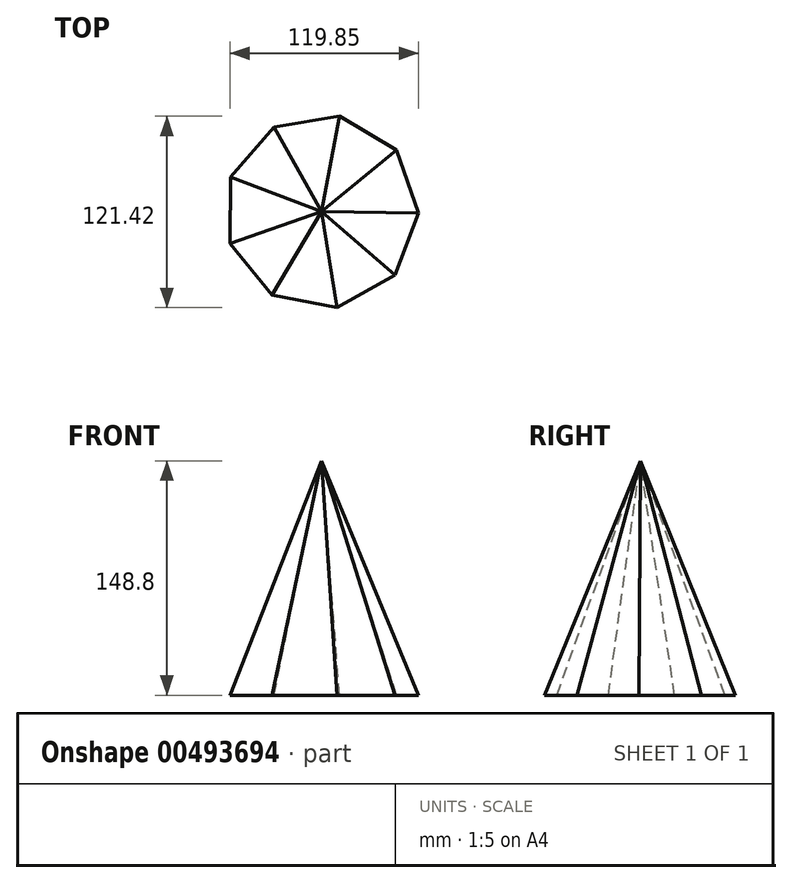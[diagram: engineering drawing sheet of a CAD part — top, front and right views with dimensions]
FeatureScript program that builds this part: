
annotation { "Feature Type Name" : "Feature", "Feature Type Description" : "" }
export const myFeature = defineFeature(function(context is Context, id is Id, definition is map)
    precondition{}
    {
        {
            var Q0;
            Q0=qCreatedBy(makeId("Top.planeOp"),FACE);
            var sketch = newSketch(context, id + "F0", { "sketchPlane" : qUnion([Q0])});
            skCircle(sketch, "E0.cCircle", {"center": v(0, 0) * mm, "radius": 61.65 * mm, "construction": true});
            skLineSegment(sketch, "E0.0", {"start": v(-30.12, 53.8) * mm, "end": v(11.5, 60.57) * mm});
            skLineSegment(sketch, "E0.1", {"start": v(11.5, 60.57) * mm, "end": v(47.74, 39) * mm});
            skLineSegment(sketch, "E0.2", {"start": v(47.74, 39) * mm, "end": v(61.65, -0.8) * mm});
            skLineSegment(sketch, "E0.3", {"start": v(61.65, -0.8) * mm, "end": v(46.7, -40.24) * mm});
            skLineSegment(sketch, "E0.4", {"start": v(46.7, -40.24) * mm, "end": v(9.9, -60.85) * mm});
            skLineSegment(sketch, "E0.5", {"start": v(9.9, -60.85) * mm, "end": v(-31.52, -52.98) * mm});
            skLineSegment(sketch, "E0.6", {"start": v(-31.52, -52.98) * mm, "end": v(-58.2, -20.32) * mm});
            skLineSegment(sketch, "E0.7", {"start": v(-58.2, -20.32) * mm, "end": v(-57.65, 21.84) * mm});
            skLineSegment(sketch, "E0.8", {"start": v(-57.65, 21.84) * mm, "end": v(-30.12, 53.8) * mm});
            skSolve(sketch);
        }
        {
            var Q0;
            Q0=qCreatedBy(makeId("Top.planeOp"),FACE);
            cPlane(context, id + "F1", {"entities" : qUnion([Q0]), "cplaneType" : CPlaneType.OFFSET, "offset" : 148.8 * mm, "width" : 150 * mm, "height" : 150 * mm});
        }
        {
            var Q0;
            Q0=qCreatedBy(id+"F1.planeOp",FACE);
            var sketch = newSketch(context, id + "F2", { "sketchPlane" : qUnion([Q0])});
            skPoint(sketch, "E1", {"position": v(0, 0) * mm});
            skSolve(sketch);
        }
        {
            var Q0;
            Q0=makeQuery(id+"F0.imprint","IMPRINT",FACE,{"disambiguationData":[TD([[makeQuery(id+"F0.imprint","IMPRINT",EDGE,{"derivedFrom":sQuery(id+"F0.wireOp",EDGE,"E0.0")}),-1.0]])]});
            var Q1;
            Q1=sQuery(id+"F2.wireOp",VERTEX,"E1");
            loft(context, id + "F3", {"sheetProfilesArray" : [{ "sheetProfileEntities" : qUnion([Q0]) }, { "sheetProfileEntities" : qUnion([Q1]) }]});
        }
    });
